# Revit family: РОСМА_МанометрВиброустойчивый
name_source: partatom
category: Арматура трубопроводов
revit_build: Autodesk Revit 2018 (Build: 20180423_1000(x64)
units: mm (PartAtom-declared; Revit-internal decimal feet)

## family parameters
Всегда вертикально = Да
На основе рабочей плоскости = Нет
Общий = Нет
При загрузке вырезать с полостями = Нет
Размер круглого соединителя = Использовать диаметр
Тип детали = Вставляется

## types (4) — shared parameters
ADSK_Единица измерения = шт.
ADSK_Количество = 1
Table = спец_виброустойчивый
Table_2 = размеры_виброустойчивый
URL = https://rosma.spb.ru
Группа модели = Оборудование
Давление01 = ‎ : ТВ -0,1…0МПа
Давление03 = ‎ : ТМ 0…0,1МПа
Давление04 = ‎ : ТМ 0…0,16МПа
Давление05 = ‎ : ТМ 0…0,25МПа
Давление06 = ‎ : ТМ 0…0,4МПа
Давление07 = ‎ : ТМ 0…0,6МПа
Давление08 = ‎ : ТМ 0…1,0МПа
Давление09 = ‎ : ТМ 0…1,6МПа
Давление10 = ‎ : ТМ 0…2,5МПа
Давление11 = ‎ : ТМ 0…4МПа
Давление12 = ‎ : ТМ 0…6МПа
Давление13 = ‎ : ТМ 0…10МПа
Давление14 = ‎ : ТМ 0…16МПа
Давление15 = ‎ : ТМ 0…25МПа
Давление16 = ‎ : ТМ 0…40МПа
Давление17 = ‎ : ТМ 0…60МПа
Давление18 = ‎ : ТМ 0…100МПа
Давление19 = ‎ : ТМВ -0,1…0,15МПа
Давление20 = ‎ : ТМВ -0,1…0,3МПа
Давление21 = ‎ : ТМВ -0,1…0,5МПа
Давление22 = ‎ : ТМВ -0,1…0,9МПа
Давление23 = ‎ : ТМВ -0,1…1,5МПа
Давление24 = ‎ : ТМВ -0,1…2,4МПа
Изготовитель = ЗАО "РОСМА"
Климатическое исполнение = Группа Д2; климатическое исполнение УХЛ кат. 1.1
Код IP = IP65
Межповерочный интервал = 2 года
Описание = Манометр показывающий ТМ серия 20, с возможностью гидрозаполнения (виброустойчивый), в корпусе из нержавеющей стали.
Техническая документация = ТУ 4212-001-4719015564-2008; ГОСТ 2405–88

## per-type parameters (varying)
| type | Ddempfer | Класс точности | Объем заполняемой жидкости | лого_задн_стенка |
| 620 | 6 мм | 1,0 | 770 мл | Да |
| 320 | 5 мм | 1,5 | 90 мл | Да |
| 220 | 5 мм | 2,5 | 80 мл | Нет |
| 520 | 6 мм | 1,0 | 350 мл | Да |

note: column(s) folded — value = type name in every type: Исполнение
